# Revit family: TY3334
name_source: partatom
category: Sprinklers
revit_build: Autodesk Revit 2016 (Build: 20150220_1215(x64)
units: mm (PartAtom-declared; Revit-internal decimal feet)

## family parameters
Always vertical = Yes
Cut with Voids When Loaded = No
Maintain Annotation Orientation = No
OmniClass Number = 23.65.70.17.11.24
OmniClass Title = Fire Fighting Sprinkler Heads
Part Type = Normal
Room Calculation Point = No
Round Connector Dimension = Use Diameter
Shared = No
Work Plane-Based = No

## types (8) — shared parameters
COBie = Yes
COBie.Component.Name = Sprinklers:Sidewall_SIN
COBie.Type = Yes
COBie.Type.AssetType = Fixed
COBie.Type.Category = Pr_70_55_97_84:Sprinklers
COBie.Type.DurationUnit = year
COBie.Type.Manufacturer = Tyco Fire Protection Products
COBie.Type.Material = Brass
COBie.Type.NominalHeight = 0' - 0"
COBie.Type.NominalLength = 0' - 0"
COBie.Type.NominalWidth = 0' - 0"
COBie.Type.Shape = Cylinder
COBie.Type.WarrantyGuarantorParts = http://tycofsbp.com
Coverage = Standard
K-Factor = 5.5493
Manufacturer = Tyco Fire Protection Products
Manufacturer URL = www.tyco-fire.com
Model = LFII
Nominal Diameter 1 = 1"
Orifice = Standard
Orifice Size = 0"
Outside Diameter 1 = 1"
Response = Quick
SIN No = TY3334
Takeout 1 = 2"
Technical Data Sheet No = TFP415
zero-valued in all types: COBie.Type.ReplacementCost, Style Id

## per-type parameters (varying)
| type | COBie.Component.Description | COBie.Type.Colour | COBie.Type.Finish | COBie.Type.ModelNumber | COBie.Type.ModelReference | COBie.Type.Size | Part No | Temperature Rating |
| #LFII, Residl, NFPA 13 Optimized HSW Sprinklers 1/2" NPT K=5.6 155°F (68°C) Brass TY3334 TFP415_51-524-1-155 | LFII Wet Sidewall  68.3°C K80 DN15 NPT Br | Yellow | Natural Brass | 51-524-1-155 | LFII Wet Sidewall  68.3°C K80 DN15 NPT Br | 1/2'(DN15) | 51-524-1-155 | 155 °F |
| #LFII, Residl, NFPA 13 Optimized HSW Sprinklers 1/2" NPT K=5.6 175°F (79°C) Brass TY3334 TFP415_51-524-1-175 | LFII Wet Sidewall  79.4°C K80 DN15 NPT Br | Yellow | Natural Brass | 51-524-1-175 | LFII Wet Sidewall  79.4°C K80 DN15 NPT Br | 1/2"(DN15) | 51-524-1-175 | 175 °F |
| LFII 1/2 K5.6 155 RAL 9010 HSW,_51-524-3-155 | LFII Wet Sidewall  68.3°C K80 DN15 NPT Wh9010 | White | Pure White | 51-524-3-155 | LFII Wet Sidewall  68.3°C K80 DN15 NPT Wh9010 | 1/2"(DN15) | 51-524-3-155 | 155 °F |
| LFII 1/2 K5.6 175 RAL 9010 HSW,_51-524-3-175 | LFII Wet Sidewall  79.4°C K80 DN15 NPT Wh9010 | White | Signal White | 51-524-3-175 | LFII Wet Sidewall  79.4°C K80 DN15 NPT Wh9010 | 1/2"(DN15) | 51-524-3-175 | 175 °F |
| #LFII, Residl, NFPA 13 Optimized HSW Sprinklers 1/2" NPT K=5.6 155°F (68°C)  White TY3334 TFP415_51-524-4-155 | LFII Wet Sidewall  68.3°C K80 DN15 NPT Wh | White | Pure White | 51-524-4-155 | LFII Wet Sidewall  68.3°C K80 DN15 NPT Wh | 1/2"(DN15) | 51-524-4-155 | 155 °F |
| #LFII, Residl, NFPA 13 Optimized HSW Sprinklers 1/2" NPT K=5.6 175°F (79°C  White TY3334 TFP415_51-524-4-175 | LFII Wet Sidewall  79.4°C K80 DN15 NPT Wh | White | Pure White | 51-524-4-175 | LFII Wet Sidewall  79.4°C K80 DN15 NPT Wh | 1/2"(DN15) | 51-524-4-175 | 175 °F |
| #LFII, Residl, NFPA 13 Optimized HSW Sprinklers 1/2" NPT K=5.6 155°F (68°C)  Chrome TY3334 TFP415_51-524-9-155 | LFII Wet Sidewall  68.3°C K80 DN15 NPT Chr | Silver | Chrome plated | 51-524-9-155 | LFII Wet Sidewall  68.3°C K80 DN15 NPT Chr | 1/2"(DN15) | 51-524-9-155 | 155 °F |
| #LFII, Residl, NFPA 13 Optimized HSW Sprinklers 1/2" NPT K=5.6 175°F (79°C  Chrome TY3334 TFP415_51-524-9-175 | LFII Wet Sidewall  79.4°C K80 DN15 NPT Chr | Silver | Chrome Plated | 51-524-9-175 | LFII Wet Sidewall  79.4°C K80 DN15 NPT Chr | 1/2"(DN15) | 51-524-9-175 | 175 °F |

note: column(s) folded — value = type name in every type: Description

## geometry (parser evidence)
native form markers: Blend x2, Sweep x48
no freeform markers — native parametric forms only
